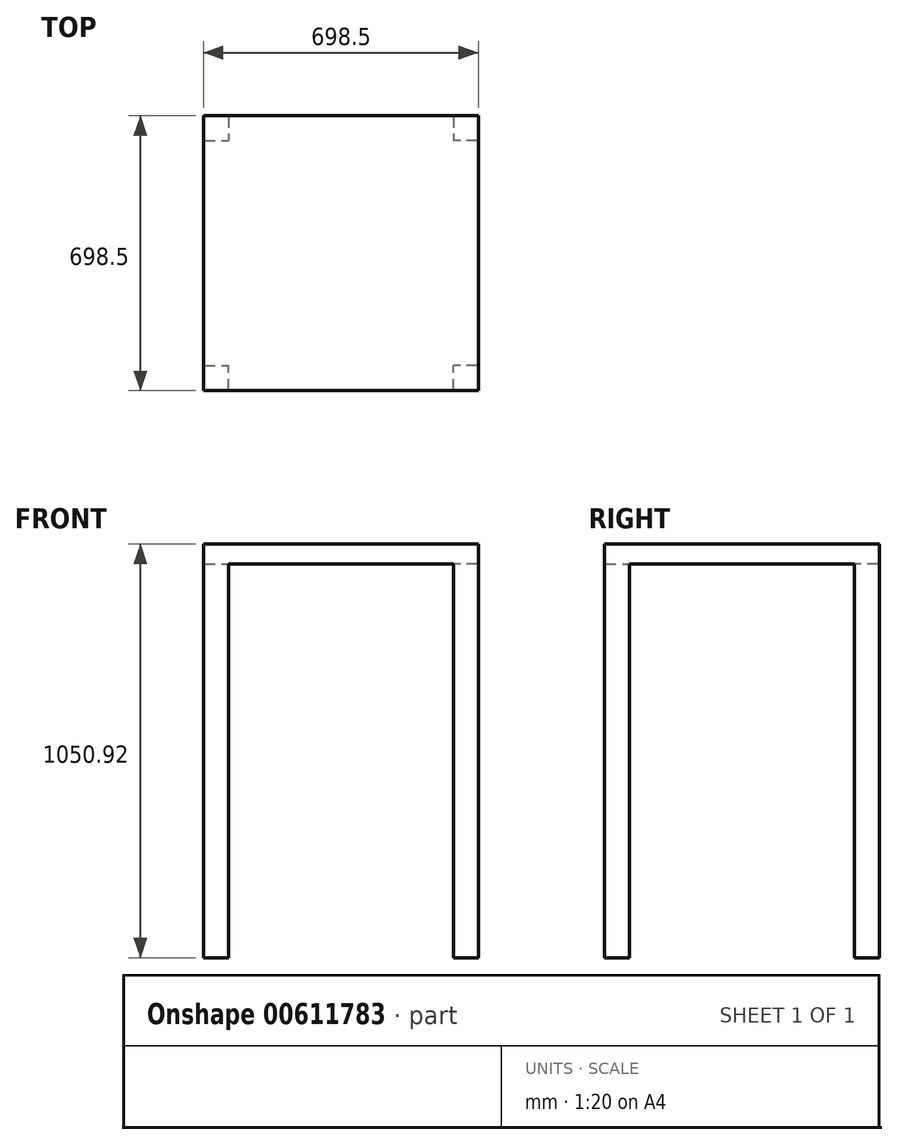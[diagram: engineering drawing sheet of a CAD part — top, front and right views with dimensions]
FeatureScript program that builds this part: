
annotation { "Feature Type Name" : "Feature", "Feature Type Description" : "" }
export const myFeature = defineFeature(function(context is Context, id is Id, definition is map)
    precondition{}
    {
        {
            var Q0;
            Q0=qCreatedBy(makeId("Top.planeOp"),FACE);
            var sketch = newSketch(context, id + "F0", { "sketchPlane" : qUnion([Q0])});
            skLineSegment(sketch, "E0.bottom", {"start": v(-356.51, 413.83) * mm, "end": v(341.99, 413.83) * mm});
            skLineSegment(sketch, "E0.top", {"start": v(-356.51, -284.67) * mm, "end": v(341.99, -284.67) * mm});
            skLineSegment(sketch, "E0.left", {"start": v(-356.51, 413.83) * mm, "end": v(-356.51, -284.67) * mm});
            skLineSegment(sketch, "E0.right", {"start": v(341.99, 413.83) * mm, "end": v(341.99, -284.67) * mm});
            skSolve(sketch);
        }
        {
            var Q0;
            Q0=makeQuery(id+"F0.imprint","IMPRINT",FACE,{"disambiguationData":[TD([[makeQuery(id+"F0.imprint","IMPRINT",EDGE,{"derivedFrom":sQuery(id+"F0.wireOp",EDGE,"E0.bottom")}),-1.0]])]});
            extrude(context, id + "F1", {"entities" : qUnion([Q0]), "depth" : 50.8 * mm, "offsetDistance" : 25.4 * mm});
        }
        {
            var Q0;
            Q0=makeQuery(id+"F1.opExtrude","CAP_FACE",FACE,{"disambiguationData":[OSD([sQuery(id+"F0.wireOp",EDGE,"E0.bottom"),sQuery(id+"F0.wireOp",EDGE,"E0.top"),sQuery(id+"F0.wireOp",EDGE,"E0.left"),sQuery(id+"F0.wireOp",EDGE,"E0.right")])],"isStart":true});
            var sketch = newSketch(context, id + "F2", { "sketchPlane" : qUnion([Q0])});
            skLineSegment(sketch, "E1.bottom", {"start": v(-356.51, 284.67) * mm, "end": v(-293.01, 284.67) * mm});
            skLineSegment(sketch, "E1.top", {"start": v(-356.51, 221.17) * mm, "end": v(-293.01, 221.17) * mm});
            skLineSegment(sketch, "E1.left", {"start": v(-356.51, 284.67) * mm, "end": v(-356.51, 221.17) * mm});
            skLineSegment(sketch, "E1.right", {"start": v(-293.01, 284.67) * mm, "end": v(-293.01, 221.17) * mm});
            skLineSegment(sketch, "E2", {"start": v(-7.26, 284.67) * mm, "end": v(-7.26, -413.83) * mm, "construction": true});
            skLineSegment(sketch, "E3", {"start": v(341.99, -64.58) * mm, "end": v(-356.51, -64.58) * mm, "construction": true});
            skLineSegment(sketch, "E4.MirrorCS", {"start": v(341.99, 284.67) * mm, "end": v(278.49, 284.67) * mm});
            skLineSegment(sketch, "E5.MirrorCS", {"start": v(341.99, 221.17) * mm, "end": v(278.49, 221.17) * mm});
            skLineSegment(sketch, "E6.MirrorCS", {"start": v(278.49, 284.67) * mm, "end": v(278.49, 221.17) * mm});
            skLineSegment(sketch, "E7.MirrorCS", {"start": v(341.99, 284.67) * mm, "end": v(341.99, 221.17) * mm});
            skLineSegment(sketch, "E8.MirrorCS", {"start": v(-356.51, -350.33) * mm, "end": v(-293.01, -350.33) * mm});
            skLineSegment(sketch, "E9.MirrorCS", {"start": v(-293.01, -413.83) * mm, "end": v(-293.01, -350.33) * mm});
            skLineSegment(sketch, "E10.MirrorCS", {"start": v(278.49, -413.83) * mm, "end": v(278.49, -350.33) * mm});
            skLineSegment(sketch, "E11.MirrorCS", {"start": v(341.99, -413.83) * mm, "end": v(278.49, -413.83) * mm});
            skLineSegment(sketch, "E12.MirrorCS", {"start": v(-356.51, -413.83) * mm, "end": v(-293.01, -413.83) * mm});
            skLineSegment(sketch, "E13.MirrorCS", {"start": v(341.99, -350.33) * mm, "end": v(278.49, -350.33) * mm});
            skLineSegment(sketch, "E14.MirrorCS", {"start": v(-356.51, -413.83) * mm, "end": v(-356.51, -350.33) * mm});
            skLineSegment(sketch, "E15.MirrorCS", {"start": v(341.99, -413.83) * mm, "end": v(341.99, -350.33) * mm});
            skSolve(sketch);
        }
        {
            var Q0;
            Q0 = qSketchRegion(id + "F2", true);
            extrude(context, id + "F3", {"entities" : qUnion([Q0]), "operationType" : NewBodyOperationType.ADD, "depth" : 1000.12 * mm, "offsetDistance" : 25.4 * mm});
        }
    });
